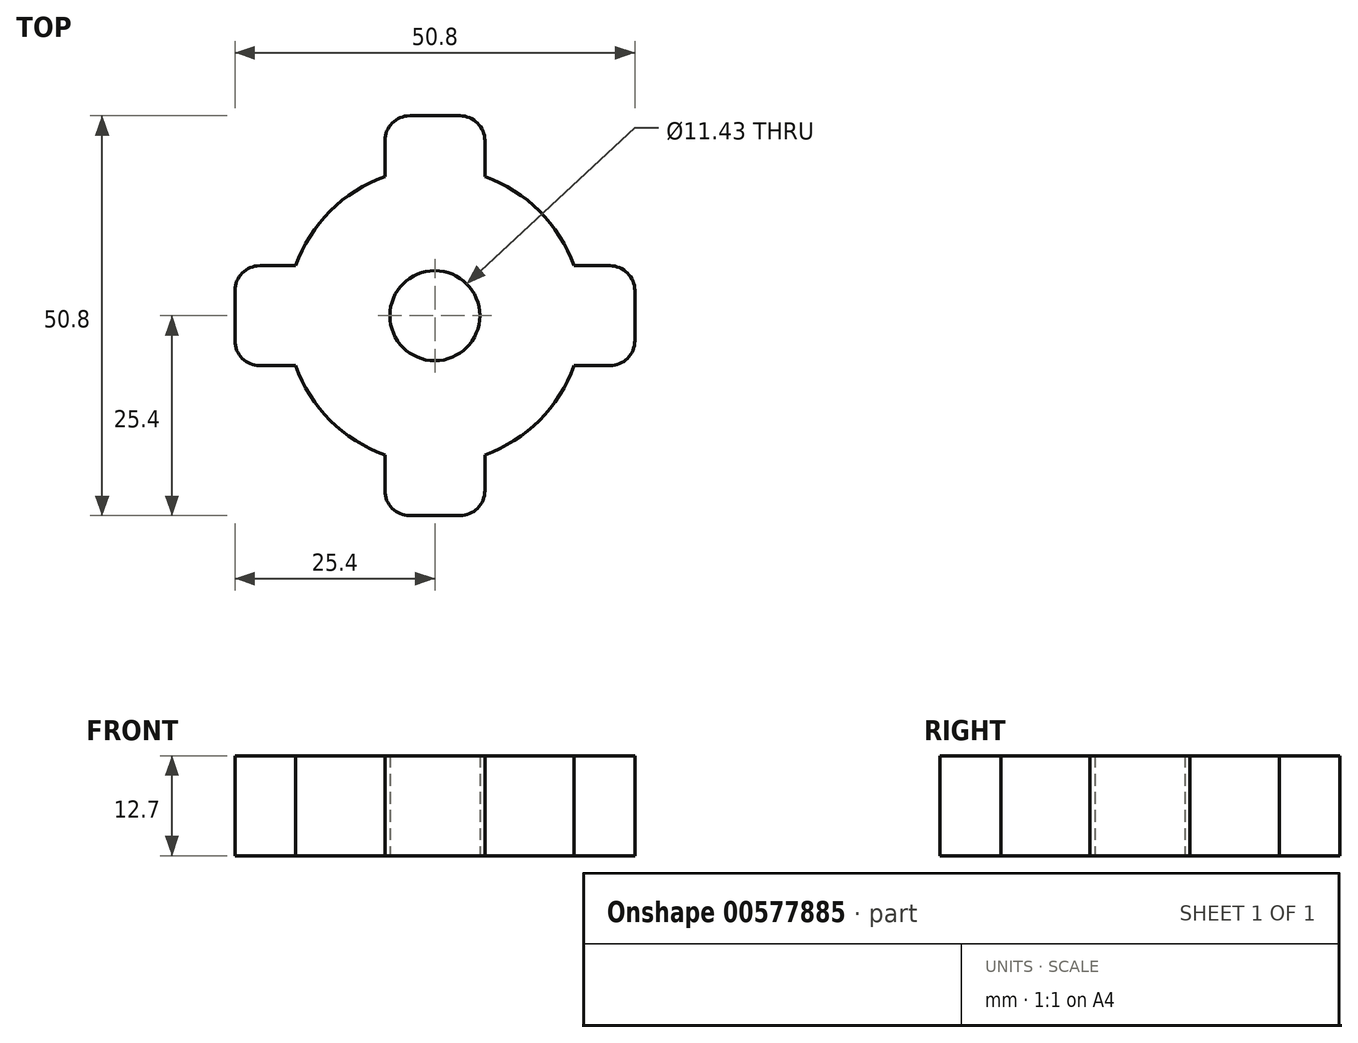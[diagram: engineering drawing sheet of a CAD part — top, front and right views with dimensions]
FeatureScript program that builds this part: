
annotation { "Feature Type Name" : "Feature", "Feature Type Description" : "" }
export const myFeature = defineFeature(function(context is Context, id is Id, definition is map)
    precondition{}
    {
        {
            var Q0;
            Q0=qCreatedBy(makeId("Top.planeOp"),FACE);
            var sketch = newSketch(context, id + "F0", { "sketchPlane" : qUnion([Q0])});
            skCircle(sketch, "E0", {"center": v(0, 0) * mm, "radius": 5.72 * mm});
            skCircle(sketch, "E1", {"center": v(0, 0) * mm, "radius": 7.94 * mm});
            skCircle(sketch, "E2", {"center": v(0, 0) * mm, "radius": 18.8 * mm});
            skLineSegment(sketch, "E3.bottom", {"start": v(22.23, -6.35) * mm, "end": v(17.7, -6.35) * mm});
            skLineSegment(sketch, "E3.top", {"start": v(22.23, 6.35) * mm, "end": v(17.7, 6.35) * mm});
            skLineSegment(sketch, "E3.left", {"start": v(25.4, -3.17) * mm, "end": v(25.4, 3.18) * mm});
            skLineSegment(sketch, "E3.right", {"start": v(-25.4, -3.18) * mm, "end": v(-25.4, 3.17) * mm});
            skPoint(sketch, "E4.visualSharp", {"position": v(-25.4, 6.35) * mm});
            skArc(sketch, "E4.filletArc", {"start": v(-22.23, 6.35) * mm, "mid": v(-24.47, 5.42) * mm, "end": v(-25.4, 3.17) * mm});
            skPoint(sketch, "E5.visualSharp", {"position": v(-25.4, -6.35) * mm});
            skArc(sketch, "E5.filletArc", {"start": v(-25.4, -3.18) * mm, "mid": v(-24.47, -5.42) * mm, "end": v(-22.23, -6.35) * mm});
            skPoint(sketch, "E6.visualSharp", {"position": v(25.4, -6.35) * mm});
            skArc(sketch, "E6.filletArc", {"start": v(22.23, -6.35) * mm, "mid": v(24.47, -5.42) * mm, "end": v(25.4, -3.17) * mm});
            skPoint(sketch, "E7.visualSharp", {"position": v(25.4, 6.35) * mm});
            skArc(sketch, "E7.filletArc", {"start": v(25.4, 3.18) * mm, "mid": v(24.47, 5.42) * mm, "end": v(22.23, 6.35) * mm});
            skPoint(sketch, "E8.1.0", {"position": v(-6.35, 25.4) * mm});
            skPoint(sketch, "E8.1.1", {"position": v(6.35, 25.4) * mm});
            skArc(sketch, "E8.1.2", {"start": v(-3.18, 25.4) * mm, "mid": v(-5.42, 24.47) * mm, "end": v(-6.35, 22.23) * mm});
            skArc(sketch, "E8.1.3", {"start": v(6.35, 22.23) * mm, "mid": v(5.42, 24.47) * mm, "end": v(3.17, 25.4) * mm});
            skLineSegment(sketch, "E8.1.4", {"start": v(-3.18, 25.4) * mm, "end": v(3.17, 25.4) * mm});
            skPoint(sketch, "E8.1.5", {"position": v(-6.35, -25.4) * mm});
            skLineSegment(sketch, "E8.1.6", {"start": v(-3.17, -25.4) * mm, "end": v(3.18, -25.4) * mm});
            skArc(sketch, "E8.1.7", {"start": v(-6.35, -22.23) * mm, "mid": v(-5.42, -24.47) * mm, "end": v(-3.17, -25.4) * mm});
            skArc(sketch, "E8.1.8", {"start": v(3.18, -25.4) * mm, "mid": v(5.42, -24.47) * mm, "end": v(6.35, -22.23) * mm});
            skPoint(sketch, "E8.1.9", {"position": v(6.35, -25.4) * mm});
            skLineSegment(sketch, "E8.1.10", {"start": v(-6.35, -22.23) * mm, "end": v(-6.35, -17.7) * mm});
            skLineSegment(sketch, "E8.1.11", {"start": v(6.35, -22.23) * mm, "end": v(6.35, -17.7) * mm});
            skLineSegment(sketch, "E8.anchor1", {"start": v(0, 0) * mm, "end": v(-25.4, -6.35) * mm, "construction": true});
            skLineSegment(sketch, "E8.anchor2", {"start": v(0, 0) * mm, "end": v(-6.35, 25.4) * mm, "construction": true});
            skLineSegment(sketch, "E9.trimOffspring", {"start": v(-6.35, 17.7) * mm, "end": v(-6.35, 22.23) * mm});
            skLineSegment(sketch, "E10.trimOffspring", {"start": v(-17.7, 6.35) * mm, "end": v(-22.23, 6.35) * mm});
            skLineSegment(sketch, "E11.trimOffspring", {"start": v(-17.7, -6.35) * mm, "end": v(-22.23, -6.35) * mm});
            skLineSegment(sketch, "E12.trimOffspring", {"start": v(6.35, 17.7) * mm, "end": v(6.35, 22.23) * mm});
            skSolve(sketch);
        }
        {
            var Q0;
            Q0=makeQuery(id+"F0.imprint","IMPRINT",FACE,{"disambiguationData":[TD([[makeQuery(id+"F0.imprint","IMPRINT",EDGE,{"derivedFrom":sQuery(id+"F0.wireOp",EDGE,"E3.right")}),-1.0]])]});
            var Q1;
            Q1=makeQuery(id+"F0.imprint","IMPRINT",FACE,{"disambiguationData":[TD([[makeQuery(id+"F0.imprint","IMPRINT",EDGE,{"derivedFrom":sQuery(id+"F0.wireOp",EDGE,"E1")}),-1.0]])]});
            var Q2;
            Q2=makeQuery(id+"F0.imprint","IMPRINT",FACE,{"disambiguationData":[TD([[makeQuery(id+"F0.imprint","IMPRINT",EDGE,{"derivedFrom":sQuery(id+"F0.wireOp",EDGE,"E8.1.2")}),1.0]])]});
            var Q3;
            Q3=makeQuery(id+"F0.imprint","IMPRINT",FACE,{"disambiguationData":[TD([[makeQuery(id+"F0.imprint","IMPRINT",EDGE,{"derivedFrom":sQuery(id+"F0.wireOp",EDGE,"E8.1.6")}),1.0]])]});
            var Q4;
            {var subQ1=sQuery(id+"F0.wireOp",EDGE,"E3.bottom");Q4=makeQuery(id+"F0.imprint","IMPRINT",FACE,{"disambiguationData":[TD([[makeQuery(id+"F0.imprint","IMPRINT",EDGE,{"derivedFrom":subQ1}),-1.0]])]});}
            var Q5;
            Q5=makeQuery(id+"F0.imprint","IMPRINT",FACE,{"disambiguationData":[TD([[makeQuery(id+"F0.imprint","IMPRINT",EDGE,{"derivedFrom":sQuery(id+"F0.wireOp",EDGE,"E0")}),-1.0]])]});
            extrude(context, id + "F1", {"entities" : qUnion([Q0, Q1, Q2, Q3, Q4, Q5]), "depth" : 12.7 * mm, "offsetDistance" : 25.4 * mm});
        }
    });
